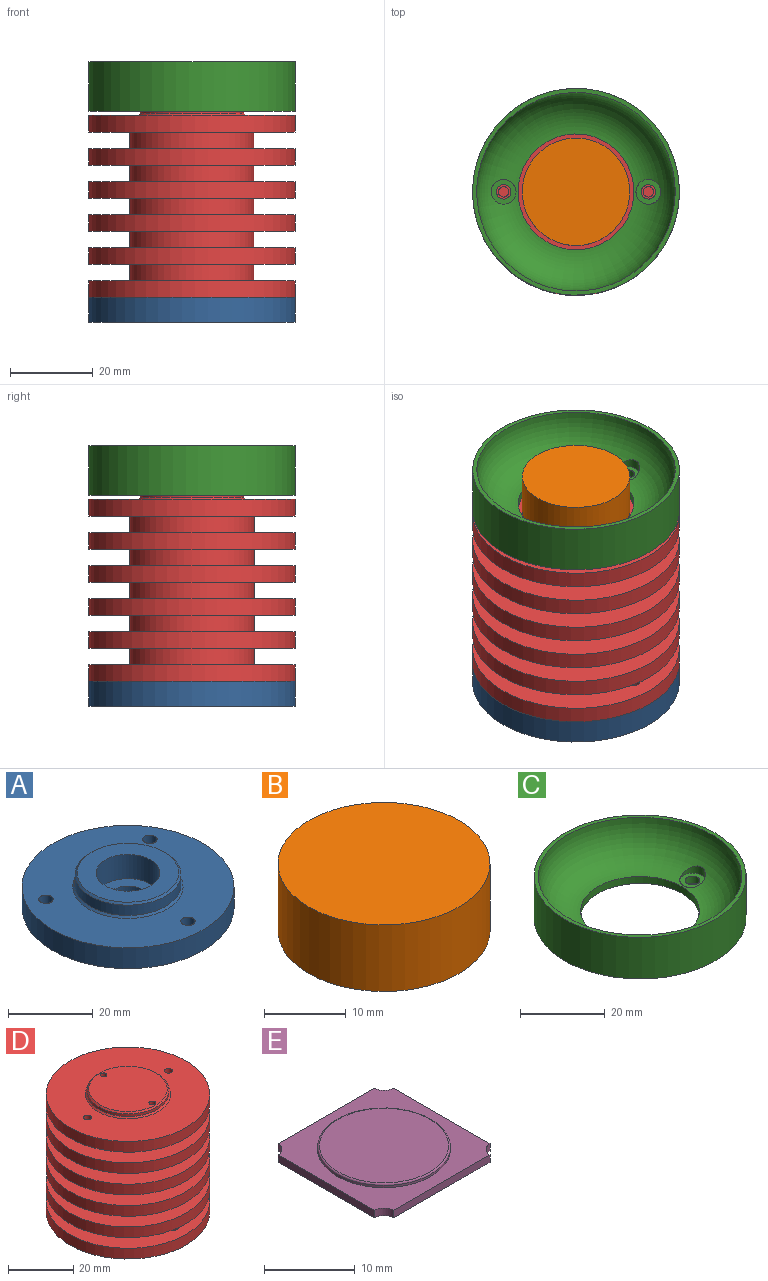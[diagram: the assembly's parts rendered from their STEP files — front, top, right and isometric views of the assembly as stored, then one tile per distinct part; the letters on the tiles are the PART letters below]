
ASSEMBLY  parts=5 mates=11
PART A: 27 faces, bbox 50x50x10 mm
  f0: cylinder r=4.5mm len=9mm, axis (0,0,-1), area 84.8mm2, adj f2,f26
  f1: cylinder r=25mm len=50mm, axis (0,0,1), area 942.5mm2, adj f2,f3
  f2: plane 50x50mm, normal (0,0,-1), area 1780.7mm2, adj f0,f1,f6,f9,f12,f18,f20,f22
  f3: plane 50x50mm, normal (0,0,1), area 1405.3mm2, adj f1,f4,f7,f10,f15
  f4: cylinder r=1.7mm len=3.4mm, axis (0,0,-1), area 32mm2, adj f3,f5
  f5: plane 6.5x6.5mm, normal (0,0,-1), area 24.1mm2, adj f4,f6
  f6: cylinder r=3.25mm len=6.5mm, axis (0,0,-1), area 61.3mm2, adj f2,f5
  f7: cylinder r=1.7mm len=3.4mm, axis (0,0,-1), area 32mm2, adj f3,f8
  f8: plane 6.5x6.5mm, normal (0,0,-1), area 24.1mm2, adj f7,f9
  f9: cylinder r=3.25mm len=6.5mm, axis (0,0,-1), area 61.3mm2, adj f2,f8
  f10: cylinder r=1.7mm len=3.4mm, axis (0,0,-1), area 32mm2, adj f3,f11
  f11: plane 6.5x6.5mm, normal (0,0,-1), area 24.1mm2, adj f10,f12
  f12: cylinder r=3.25mm len=6.5mm, axis (0,0,-1), area 61.3mm2, adj f2,f11
  f13: cylinder r=12.5mm len=25mm, axis (0,0,-1), area 235.6mm2, adj f15,f16
  f14: plane 24x24mm, normal (0,0,1), area 275.7mm2, adj f16,f25
  f15: cone r=12.5mm half-angle=45deg, axis (0,0,-1), area 56.6mm2, adj f3,f13
  f16: cone r=12mm half-angle=45deg, axis (0,0,-1), area 54.4mm2, adj f13,f14
  f17: cone r=0mm half-angle=59deg, axis (0,0,-1), area 5.7mm2, adj f18
  f18: cylinder r=1.25mm len=8.5mm, axis (0,0,-1), area 66.8mm2, adj f2,f17
  f19: cone r=0mm half-angle=59deg, axis (0,0,-1), area 5.7mm2, adj f20
  f20: cylinder r=1.25mm len=8.5mm, axis (0,0,-1), area 66.8mm2, adj f2,f19
  f21: cone r=0mm half-angle=59deg, axis (0,0,-1), area 5.7mm2, adj f22
  f22: cylinder r=1.25mm len=8.5mm, axis (0,0,-1), area 66.8mm2, adj f2,f21
  f23: cone r=0mm half-angle=59deg, axis (0,0,-1), area 5.7mm2, adj f24
  f24: cylinder r=1.25mm len=8.5mm, axis (0,0,-1), area 66.8mm2, adj f2,f23
  f25: cylinder r=7.5mm len=15mm, axis (0,0,1), area 329.9mm2, adj f14,f26
  f26: plane 15x15mm, normal (0,0,1), area 113.1mm2, adj f0,f25
PART B: 5 faces, bbox 26x26x10 mm
  f0: cylinder r=13mm len=26mm, axis (0,0,-1), area 816.8mm2, adj f1,f2
  f1: plane 26x26mm, normal (0,0,1), area 530.9mm2, adj f0
  f2: plane 26x26mm, normal (0,0,-1), area 78.5mm2, adj f0,f3
  f3: cylinder r=12mm len=24mm, axis (0,0,-1), area 150.8mm2, adj f2,f4
  f4: plane 24x24mm, normal (0,0,-1), area 452.4mm2, adj f3
PART C: 11 faces, bbox 52x52x19.1 mm
  f0: torus R=14mm, axis (0,0,1), area 1948.3mm2, adj f1,f3,f7,f10
  f1: cylinder r=14mm len=28mm, axis (0,0,1), area 175.9mm2, adj f0,f4
  f2: cylinder r=25mm len=50mm, axis (0,0,-1), area 1885mm2, adj f3,f4
  f3: plane 50x50mm, normal (0,0,1), area 153.9mm2, adj f0,f2
  f4: plane 50x50mm, normal (0,0,-1), area 1328.5mm2, adj f1,f2,f5,f8
  f5: cylinder r=1.75mm len=3.5mm, axis (0,0,1), area 22mm2, adj f4,f6
  f6: plane 6x6mm, normal (0,0,1), area 18.7mm2, adj f5,f7
  f7: cylinder r=3mm len=6mm, axis (0,0,1), area 18.2mm2, adj f0,f6
  f8: cylinder r=1.75mm len=3.5mm, axis (0,0,1), area 22mm2, adj f4,f9
  f9: plane 6x6mm, normal (0,0,1), area 18.7mm2, adj f8,f10
  f10: cylinder r=3mm len=6mm, axis (0,0,1), area 18.2mm2, adj f0,f9
PART D: 37 faces, bbox 50x50x46 mm
  f0: plane 25x25mm, normal (0,0,-1), area 484.6mm2, adj f1,f25,f26
  f1: cylinder r=12.5mm len=28.5mm, axis (0,0,-1), area 2238.4mm2, adj f0,f34
  f2: plane 50x50mm, normal (0,0,-1), area 1417.8mm2, adj f3,f29,f30,f31,f34
  f3: cylinder r=25mm len=50mm, axis (0,0,-1), area 628.3mm2, adj f2,f4
  f4: plane 50x50mm, normal (0,0,1), area 1241.9mm2, adj f3,f5,f29,f30,f31
  f5: cylinder r=15mm len=30mm, axis (0,0,-1), area 377mm2, adj f4,f6
  f6: plane 50x50mm, normal (0,0,-1), area 1256.6mm2, adj f5,f7
  f7: cylinder r=25mm len=50mm, axis (0,0,-1), area 628.3mm2, adj f6,f8
  f8: plane 50x50mm, normal (0,0,1), area 1256.6mm2, adj f7,f9
  f9: cylinder r=15mm len=30mm, axis (0,0,-1), area 377mm2, adj f8,f10
  f10: plane 50x50mm, normal (0,0,-1), area 1256.6mm2, adj f9,f11
  f11: cylinder r=25mm len=50mm, axis (0,0,-1), area 628.3mm2, adj f10,f12
  f12: plane 50x50mm, normal (0,0,1), area 1256.6mm2, adj f11,f13
  f13: cylinder r=15mm len=30mm, axis (0,0,-1), area 377mm2, adj f12,f14
  f14: plane 50x50mm, normal (0,0,-1), area 1256.6mm2, adj f13,f15
  f15: cylinder r=25mm len=50mm, axis (0,0,-1), area 628.3mm2, adj f14,f16
  f16: plane 50x50mm, normal (0,0,1), area 1256.6mm2, adj f15,f17
  f17: cylinder r=15mm len=30mm, axis (0,0,-1), area 377mm2, adj f16,f18
  f18: plane 50x50mm, normal (0,0,-1), area 1256.6mm2, adj f17,f19
  f19: cylinder r=25mm len=50mm, axis (0,0,-1), area 628.3mm2, adj f18,f20
  f20: plane 50x50mm, normal (0,0,1), area 1256.6mm2, adj f19,f21
  f21: cylinder r=15mm len=30mm, axis (0,0,-1), area 377mm2, adj f20,f22
  f22: plane 50x50mm, normal (0,0,-1), area 1246.8mm2, adj f21,f23,f27,f28
  f23: cylinder r=25mm len=50mm, axis (0,0,-1), area 628.3mm2, adj f22,f24
  f24: plane 50x50mm, normal (0,0,1), area 1422.7mm2, adj f23,f27,f28,f36
  f25: cylinder r=1mm len=17mm, axis (0,0,1), area 106.8mm2, adj f0,f33
  f26: cylinder r=1mm len=17mm, axis (0,0,1), area 106.8mm2, adj f0,f33
  f27: cylinder r=1.25mm len=4mm, axis (0,0,1), area 31.4mm2, adj f22,f24
  f28: cylinder r=1.25mm len=4mm, axis (0,0,1), area 31.4mm2, adj f22,f24
  f29: cylinder r=1.25mm len=4mm, axis (0,0,-1), area 31.4mm2, adj f2,f4
  f30: cylinder r=1.25mm len=4mm, axis (0,0,-1), area 31.4mm2, adj f2,f4
  f31: cylinder r=1.25mm len=4mm, axis (0,0,-1), area 31.4mm2, adj f2,f4
  f32: cylinder r=12.5mm len=25mm, axis (0,0,-1), area 78.5mm2, adj f35,f36
  f33: plane 24x24mm, normal (0,0,1), area 446.1mm2, adj f25,f26,f35
  f34: cone r=12.5mm half-angle=45deg, axis (0,0,-1), area 56.6mm2, adj f1,f2
  f35: cone r=12mm half-angle=45deg, axis (0,0,-1), area 54.4mm2, adj f32,f33
  f36: cone r=12.5mm half-angle=45deg, axis (0,0,-1), area 56.6mm2, adj f24,f32
PART E: 13 faces, bbox 18x18x1.5 mm
  f0: plane 15x1mm, normal (-1,0,0), area 15mm2, adj f4,f5,f6,f8
  f1: plane 15x1mm, normal (0,-1,0), area 15mm2, adj f4,f5,f7,f8
  f2: plane 15x1mm, normal (1,0,0), area 15mm2, adj f4,f5,f7,f9
  f3: plane 15x1mm, normal (0,1,0), area 15mm2, adj f4,f5,f6,f9
  f4: plane 18x18mm, normal (0,0,1), area 148.9mm2, adj f0,f1,f2,f3,f6,f7,f8,f9
  f5: plane 18x18mm, normal (0,0,-1), area 316.9mm2, adj f0,f1,f2,f3,f6,f7,f8,f9
  f6: cylinder r=1.5mm len=1.5mm, axis (0,0,1), area 2.4mm2, adj f0,f3,f4,f5
  f7: cylinder r=1.5mm len=1.5mm, axis (0,0,1), area 2.4mm2, adj f1,f2,f4,f5
  f8: cylinder r=1.5mm len=1.5mm, axis (0,0,1), area 2.4mm2, adj f0,f1,f4,f5
  f9: cylinder r=1.5mm len=1.5mm, axis (0,0,1), area 2.4mm2, adj f2,f3,f4,f5
  f10: cylinder r=7.31mm len=14.62mm, axis (0,0,-1), area 13.8mm2, adj f4,f12
  f11: plane 14.22x14.22mm, normal (0,0,1), area 158.9mm2, adj f12
  f12: torus R=7.11mm, axis (0,0,1), area 14.3mm2, adj f10,f11
PLACE A t=(0,0,-6.5)mm
PLACE B t=(0,0,44.5)mm
PLACE C t=(0,0,44.5)mm
PLACE D t=(0,0,-6.5)mm
PLACE E t=(-9,-9,45.5)mm
MATE parallel C.f2 <-> E.f10  axis (0,0,-1) through (0,0,44.5)mm
MATE planar E.f10 <-> D.f32  axis (0,0,-1) through (0,0,45.5)mm
MATE slider E.f10 <-> C.f0  axis (0,0,1) through (0,0,47)mm
MATE parallel C.f2 <-> E.f5  axis (0,0,-1) through (0,0,44.5)mm
MATE cylindrical D.f27 <-> C.f5  axis (0,0,1) through (-17.5,0,41.5)mm
MATE revolute A.f0 <-> D.f1  axis (0,0,1) through (0,0,-0.5)mm
MATE slider B.f0 <-> C.f0  axis (0,0,-1) through (0,0,44.5)mm
MATE planar C.f2 <-> B.f0  axis (0,0,-1) through (0,0,44.5)mm
MATE planar E.f10 <-> B.f0  axis (0,0,-1) through (0,0,45.5)mm
MATE parallel C.f2 <-> B.f0  axis (0,0,-1) through (0,0,44.5)mm
MATE cylindrical C.f8 <-> D.f28  axis (0,0,-1) through (17.5,0,44.5)mm
